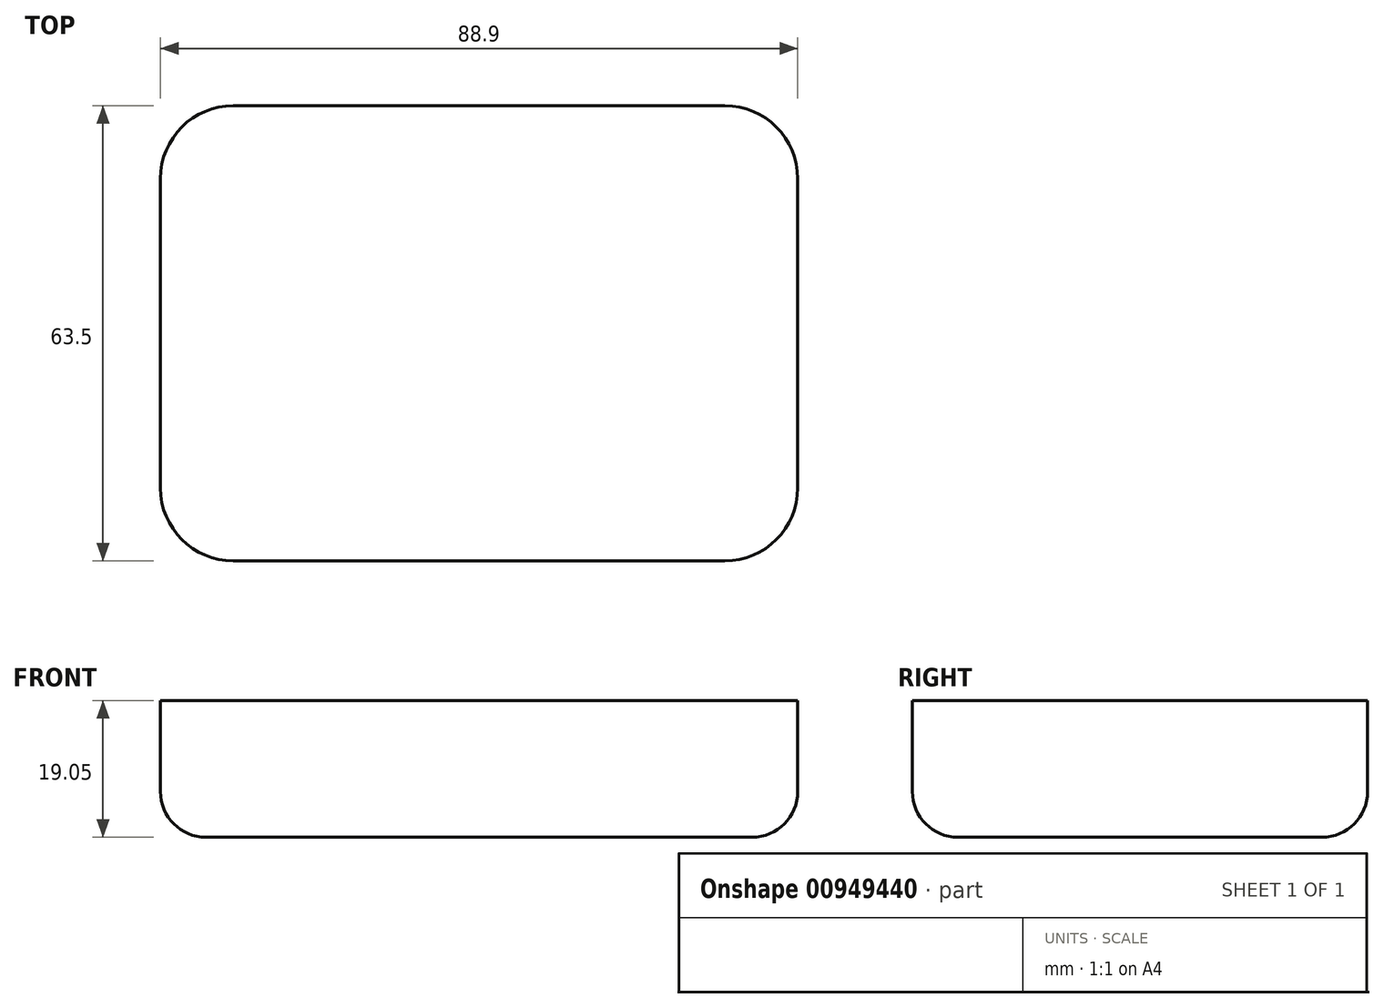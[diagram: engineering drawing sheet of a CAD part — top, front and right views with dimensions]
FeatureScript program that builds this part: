
annotation { "Feature Type Name" : "Feature", "Feature Type Description" : "" }
export const myFeature = defineFeature(function(context is Context, id is Id, definition is map)
    precondition{}
    {
        {
            var Q0;
            Q0=qCreatedBy(makeId("Top.planeOp"),FACE);
            var sketch = newSketch(context, id + "F0", { "sketchPlane" : qUnion([Q0])});
            skLineSegment(sketch, "E0.bottom", {"start": v(-34.3, 31.75) * mm, "end": v(34.29, 31.75) * mm});
            skLineSegment(sketch, "E0.top", {"start": v(-34.3, -31.75) * mm, "end": v(34.3, -31.75) * mm});
            skLineSegment(sketch, "E0.left", {"start": v(-44.45, 21.59) * mm, "end": v(-44.45, -21.6) * mm});
            skLineSegment(sketch, "E0.right", {"start": v(44.45, 21.6) * mm, "end": v(44.45, -21.6) * mm});
            skPoint(sketch, "E1.visualSharp", {"position": v(-44.45, 31.75) * mm});
            skArc(sketch, "E1.filletArc", {"start": v(-34.3, 31.75) * mm, "mid": v(-41.47, 28.77) * mm, "end": v(-44.45, 21.59) * mm});
            skPoint(sketch, "E2.visualSharp", {"position": v(-44.45, -31.75) * mm});
            skArc(sketch, "E2.filletArc", {"start": v(-44.45, -21.6) * mm, "mid": v(-41.47, -28.77) * mm, "end": v(-34.3, -31.75) * mm});
            skPoint(sketch, "E3.visualSharp", {"position": v(44.45, -31.75) * mm});
            skArc(sketch, "E3.filletArc", {"start": v(34.3, -31.75) * mm, "mid": v(41.47, -28.77) * mm, "end": v(44.45, -21.6) * mm});
            skPoint(sketch, "E4.visualSharp", {"position": v(44.45, 31.75) * mm});
            skArc(sketch, "E4.filletArc", {"start": v(44.45, 21.6) * mm, "mid": v(41.47, 28.77) * mm, "end": v(34.29, 31.75) * mm});
            skPoint(sketch, "E5.middle", {"position": v(0, 0) * mm});
            skPoint(sketch, "E6.visualSharp", {"position": v(-34.92, -22.23) * mm});
            skPoint(sketch, "E7.visualSharp", {"position": v(-34.93, 22.23) * mm});
            skPoint(sketch, "E8.visualSharp", {"position": v(34.92, 22.23) * mm});
            skPoint(sketch, "E9.visualSharp", {"position": v(34.93, -22.23) * mm});
            skSolve(sketch);
        }
        {
            var Q0;
            Q0=makeQuery(id+"F0.imprint","IMPRINT",FACE,{"disambiguationData":[TD([[makeQuery(id+"F0.imprint","IMPRINT",EDGE,{"derivedFrom":sQuery(id+"F0.wireOp",EDGE,"E0.bottom")}),-1.0]])]});
            extrude(context, id + "F1", {"entities" : qUnion([Q0]), "depth" : 19.05 * mm, "offsetDistance" : 25.4 * mm});
        }
        {
            var Q0;
            Q0=makeQuery(id+"F1.opExtrude","CAP_EDGE",EDGE,{"disambiguationData":[OSD([sQuery(id+"F0.wireOp",EDGE,"E2.filletArc")])],"isStart":true});
            fillet(context, id + "F2", {"entities" : qUnion([Q0]), "radius" : 6.35 * mm, "tangentPropagation" : true, "allowEdgeOverflow" : false});
        }
    });
